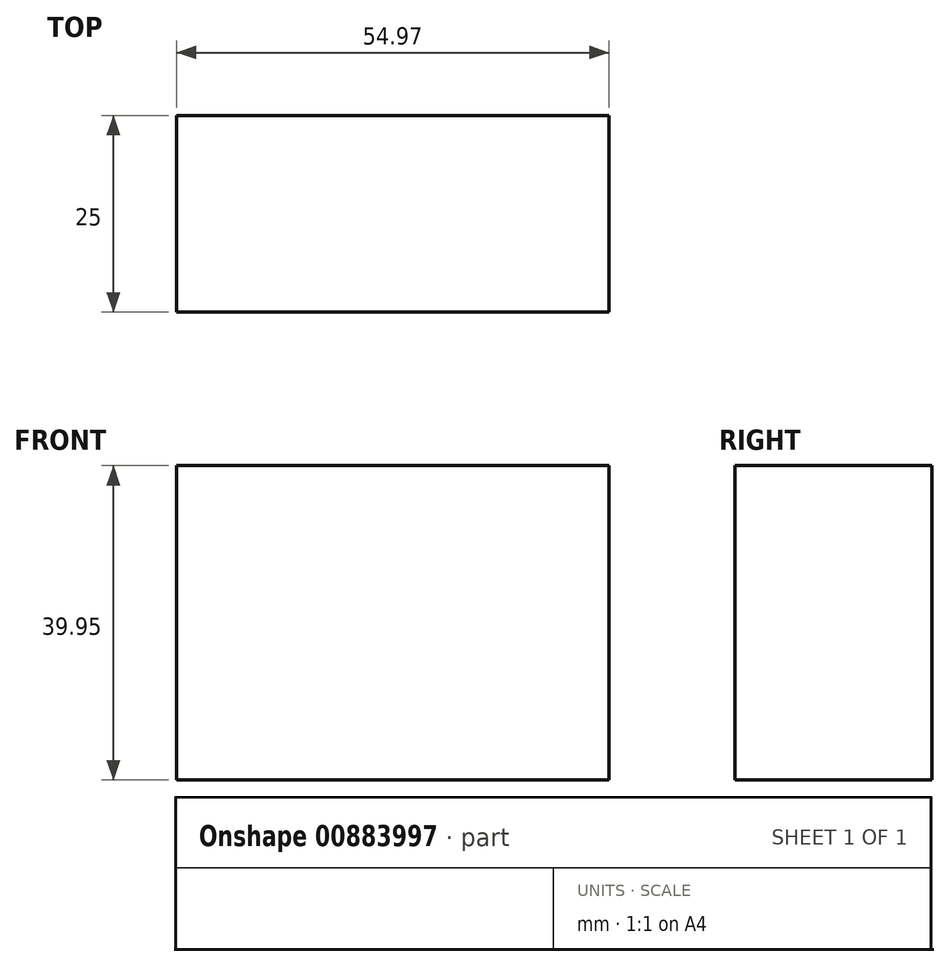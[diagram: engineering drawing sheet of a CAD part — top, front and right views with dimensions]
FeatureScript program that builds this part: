
annotation { "Feature Type Name" : "Feature", "Feature Type Description" : "" }
export const myFeature = defineFeature(function(context is Context, id is Id, definition is map)
    precondition{}
    {
        {
            assignVariable(context, id + "F0", {"name" : "as", "anyValue" : 25});
        }
        {
            var Q0;
            Q0=qCreatedBy(makeId("Front.planeOp"),FACE);
            var sketch = newSketch(context, id + "F1", { "sketchPlane" : qUnion([Q0])});
            skLineSegment(sketch, "E0.bottom", {"start": v(-85.13, 48.12) * mm, "end": v(-30.16, 48.12) * mm});
            skLineSegment(sketch, "E0.top", {"start": v(-85.13, 8.17) * mm, "end": v(-30.16, 8.17) * mm});
            skLineSegment(sketch, "E0.left", {"start": v(-85.13, 48.12) * mm, "end": v(-85.13, 8.17) * mm});
            skLineSegment(sketch, "E0.right", {"start": v(-30.16, 48.12) * mm, "end": v(-30.16, 8.17) * mm});
            skLineSegment(sketch, "E1.bottom", {"start": v(34.73, 0) * mm, "end": v(87.28, 0) * mm});
            skLineSegment(sketch, "E1.top", {"start": v(34.73, -41.97) * mm, "end": v(87.28, -41.97) * mm});
            skLineSegment(sketch, "E1.left", {"start": v(34.73, 0) * mm, "end": v(34.73, -41.97) * mm});
            skLineSegment(sketch, "E1.right", {"start": v(87.28, 0) * mm, "end": v(87.28, -41.97) * mm});
            skSolve(sketch);
        }
        {
            var Q0;
            Q0=makeQuery(id+"F1.imprint","IMPRINT",FACE,{"disambiguationData":[TD([[makeQuery(id+"F1.imprint","IMPRINT",EDGE,{"derivedFrom":sQuery(id+"F1.wireOp",EDGE,"E0.bottom")}),-1.0]])]});
            extrude(context, id + "F2", {"entities" : qUnion([Q0]), "depth" : (getVariable(context, 'as')) * mm, "offsetDistance" : 25 * mm});
        }
    });
